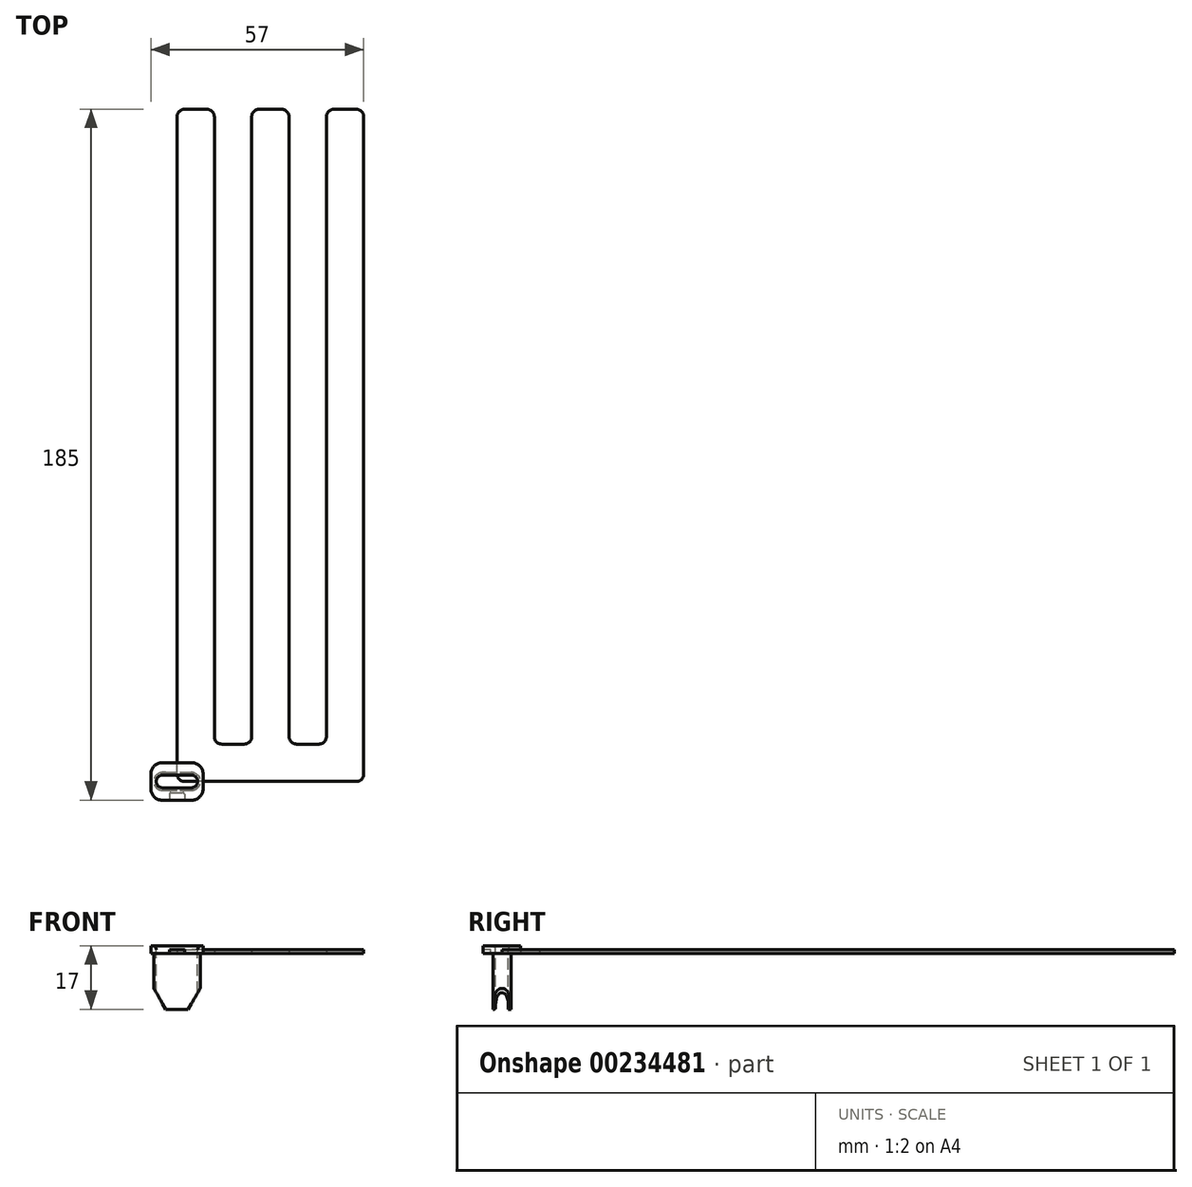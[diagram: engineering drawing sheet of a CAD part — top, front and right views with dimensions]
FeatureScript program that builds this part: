
annotation { "Feature Type Name" : "Feature", "Feature Type Description" : "" }
export const myFeature = defineFeature(function(context is Context, id is Id, definition is map)
    precondition{}
    {
        {
            var Q0;
            Q0=qCreatedBy(makeId("Top.planeOp"),FACE);
            var sketch = newSketch(context, id + "F0", { "sketchPlane" : qUnion([Q0])});
            skLineSegment(sketch, "E0", {"start": v(-3.85, 0) * mm, "end": v(3.85, 0) * mm});
            skArc(sketch, "E1.0.startCap", {"start": v(-3.85, -2.4) * mm, "mid": v(-6.25, 0) * mm, "end": v(-3.85, 2.4) * mm});
            skArc(sketch, "E1.0.endCap", {"start": v(3.85, 2.4) * mm, "mid": v(6.25, 0) * mm, "end": v(3.85, -2.4) * mm});
            skLineSegment(sketch, "E1.0.left", {"start": v(-3.85, 2.4) * mm, "end": v(3.85, 2.4) * mm});
            skLineSegment(sketch, "E1.0.right", {"start": v(-3.85, -2.4) * mm, "end": v(3.85, -2.4) * mm});
            skLineSegment(sketch, "E2.0", {"start": v(-3.85, 1.7) * mm, "end": v(3.85, 1.7) * mm});
            skArc(sketch, "E2.1", {"start": v(-3.85, -1.7) * mm, "mid": v(-5.55, 0) * mm, "end": v(-3.85, 1.7) * mm});
            skLineSegment(sketch, "E2.2", {"start": v(-3.85, -1.7) * mm, "end": v(3.85, -1.7) * mm});
            skArc(sketch, "E2.3", {"start": v(3.85, 1.7) * mm, "mid": v(5.55, 0) * mm, "end": v(3.85, -1.7) * mm});
            skSolve(sketch);
        }
        {
            var Q0;
            Q0 = qSketchRegion(id + "F0", true);
            extrude(context, id + "F1", {"entities" : qUnion([Q0]), "oppositeDirection" : true, "depth" : 15 * mm, "offsetDistance" : 25 * mm});
        }
        {
            var Q0;
            Q0=qCreatedBy(makeId("Top.planeOp"),FACE);
            var sketch = newSketch(context, id + "F2", { "sketchPlane" : qUnion([Q0])});
            skArc(sketch, "E3.0", {"start": v(-3.85, -1.7) * mm, "mid": v(-5.55, 0) * mm, "end": v(-3.85, 1.7) * mm});
            skLineSegment(sketch, "E4.0", {"start": v(-3.85, 1.7) * mm, "end": v(3.85, 1.7) * mm});
            skArc(sketch, "E5.0", {"start": v(3.85, 1.7) * mm, "mid": v(5.55, 0) * mm, "end": v(3.85, -1.7) * mm});
            skLineSegment(sketch, "E6.0", {"start": v(-3.85, -1.7) * mm, "end": v(3.85, -1.7) * mm});
            skLineSegment(sketch, "E7.bottom", {"start": v(-7, 5) * mm, "end": v(7, 5) * mm});
            skLineSegment(sketch, "E7.top", {"start": v(-7, -5) * mm, "end": v(7, -5) * mm});
            skLineSegment(sketch, "E7.left", {"start": v(-7, 5) * mm, "end": v(-7, -5) * mm});
            skLineSegment(sketch, "E7.right", {"start": v(7, 5) * mm, "end": v(7, -5) * mm});
            skPoint(sketch, "E7.middle", {"position": v(0, 0) * mm});
            skSolve(sketch);
        }
        {
            var Q0;
            Q0 = qSketchRegion(id + "F2", true);
            extrude(context, id + "F3", {"entities" : qUnion([Q0]), "operationType" : NewBodyOperationType.ADD, "depth" : 2 * mm, "offsetDistance" : 25 * mm});
        }
        {
            var Q0;
            Q0=makeQuery(id+"F3.opExtrude","SWEPT_EDGE",EDGE,{"disambiguationData":[OSD([sQuery(id+"F2.wireOp",EDGE,"E7.top"),sQuery(id+"F2.wireOp",EDGE,"E7.left")])]});
            var Q1;
            Q1=makeQuery(id+"F3.opExtrude","SWEPT_EDGE",EDGE,{"disambiguationData":[OSD([sQuery(id+"F2.wireOp",EDGE,"E7.top"),sQuery(id+"F2.wireOp",EDGE,"E7.right")])]});
            var Q2;
            Q2=makeQuery(id+"F3.opExtrude","SWEPT_EDGE",EDGE,{"disambiguationData":[OSD([sQuery(id+"F2.wireOp",EDGE,"E7.bottom"),sQuery(id+"F2.wireOp",EDGE,"E7.right")])]});
            var Q3;
            Q3=makeQuery(id+"F3.opExtrude","SWEPT_EDGE",EDGE,{"disambiguationData":[OSD([sQuery(id+"F2.wireOp",EDGE,"E7.bottom"),sQuery(id+"F2.wireOp",EDGE,"E7.left")])]});
            fillet(context, id + "F4", {"entities" : qUnion([Q0, Q1, Q2, Q3]), "tangentPropagation" : true, "radius" : 3 * mm, "defaultsChanged" : true, "vertexSettings" : [], "allowEdgeOverflow" : false});
        }
        {
            var Q0;
            Q0=qCreatedBy(makeId("Front.planeOp"),FACE);
            var sketch = newSketch(context, id + "F5", { "sketchPlane" : qUnion([Q0])});
            skLineSegment(sketch, "E8.0", {"start": v(-3.85, -15) * mm, "end": v(3.85, -15) * mm, "construction": true});
            skLineSegment(sketch, "E9", {"start": v(-3, -15) * mm, "end": v(-8.4, -5.66) * mm});
            skLineSegment(sketch, "E10", {"start": v(-8.4, -5.66) * mm, "end": v(-8.4, -15) * mm});
            skLineSegment(sketch, "E11", {"start": v(-8.4, -15) * mm, "end": v(-3, -15) * mm});
            skLineSegment(sketch, "E12", {"start": v(3, -15) * mm, "end": v(8.4, -5.66) * mm});
            skLineSegment(sketch, "E13", {"start": v(8.4, -5.66) * mm, "end": v(8.4, -15) * mm});
            skLineSegment(sketch, "E14", {"start": v(8.4, -15) * mm, "end": v(3, -15) * mm});
            skSolve(sketch);
        }
        {
            var Q0;
            Q0 = qSketchRegion(id + "F5", true);
            extrude(context, id + "F6", {"entities" : qUnion([Q0]), "operationType" : NewBodyOperationType.REMOVE, "endBound" : BoundingType.THROUGH_ALL, "oppositeDirection" : true, "depth" : 25 * mm, "offsetDistance" : 25 * mm, "hasSecondDirection" : true, "secondDirectionBound" : BoundingType.THROUGH_ALL, "secondDirectionOppositeDirection" : false, "secondDirectionDepth" : 25 * mm});
        }
        {
            var Q0;
            Q0=makeQuery(id+"F3.opExtrude","CAP_EDGE",EDGE,{"disambiguationData":[OSD([sQuery(id+"F2.wireOp",EDGE,"E3.0")])],"isStart":false});
            var Q1;
            {var subQ1=sQuery(id+"F0.wireOp",EDGE,"E1.0.right");var subQ2=sQuery(id+"F5.wireOp",EDGE,"E9");Q1=makeQuery(id+"F6.boolean.opBoolean","COPY",EDGE,{"disambiguationData":[TD([makeQuery(id+"F1.opExtrude","SWEPT_FACE",FACE,{"disambiguationData":[OSD([subQ1])]})])],"derivedFrom":makeQuery(id+"F6.opExtrude","SWEPT_EDGE",EDGE,{"disambiguationData":[OSD([subQ2,sQuery(id+"F5.wireOp",EDGE,"E11")])]})});}
            var Q2;
            {var subQ1=sQuery(id+"F0.wireOp",EDGE,"E1.0.right");var subQ2=sQuery(id+"F5.wireOp",EDGE,"E12");Q2=makeQuery(id+"F6.boolean.opBoolean","COPY",EDGE,{"disambiguationData":[TD([makeQuery(id+"F1.opExtrude","SWEPT_FACE",FACE,{"disambiguationData":[OSD([subQ1])]})])],"derivedFrom":makeQuery(id+"F6.opExtrude","SWEPT_EDGE",EDGE,{"disambiguationData":[OSD([subQ2,sQuery(id+"F5.wireOp",EDGE,"E14")])]})});}
            var Q3;
            {var subQ0=sQuery(id+"F0.wireOp",EDGE,"E1.0.left");var subQ1=sQuery(id+"F5.wireOp",EDGE,"E12");Q3=makeQuery(id+"F6.boolean.opBoolean","COPY",EDGE,{"disambiguationData":[TD([makeQuery(id+"F1.opExtrude","SWEPT_FACE",FACE,{"disambiguationData":[OSD([subQ0])]})])],"derivedFrom":makeQuery(id+"F6.opExtrude","SWEPT_EDGE",EDGE,{"disambiguationData":[OSD([subQ1,sQuery(id+"F5.wireOp",EDGE,"E14")])]})});}
            var Q4;
            {var subQ0=sQuery(id+"F0.wireOp",EDGE,"E1.0.left");var subQ2=sQuery(id+"F5.wireOp",EDGE,"E9");Q4=makeQuery(id+"F6.boolean.opBoolean","COPY",EDGE,{"disambiguationData":[TD([makeQuery(id+"F1.opExtrude","SWEPT_FACE",FACE,{"disambiguationData":[OSD([subQ0])]})])],"derivedFrom":makeQuery(id+"F6.opExtrude","SWEPT_EDGE",EDGE,{"disambiguationData":[OSD([subQ2,sQuery(id+"F5.wireOp",EDGE,"E11")])]})});}
            fillet(context, id + "F7", {"entities" : qUnion([Q0, Q1, Q2, Q3, Q4]), "tangentPropagation" : true, "radius" : 1 * mm, "defaultsChanged" : false, "vertexSettings" : [], "allowEdgeOverflow" : false});
        }
        {
            var Q0;
            Q0=makeQuery(id+"F3.opExtrude","SWEPT_FACE",FACE,{"disambiguationData":[OSD([sQuery(id+"F2.wireOp",EDGE,"E7.top")])]});
            var sketch = newSketch(context, id + "F8", { "sketchPlane" : qUnion([Q0])});
            skLineSegment(sketch, "E15.bottom", {"start": v(-2, 0) * mm, "end": v(2, 0) * mm});
            skLineSegment(sketch, "E15.top", {"start": v(-2, 1) * mm, "end": v(2, 1) * mm});
            skLineSegment(sketch, "E15.left", {"start": v(-2, 0) * mm, "end": v(-2, 1) * mm});
            skLineSegment(sketch, "E15.right", {"start": v(2, 0) * mm, "end": v(2, 1) * mm});
            skSolve(sketch);
        }
        {
            var Q0;
            Q0 = qSketchRegion(id + "F8", true);
            extrude(context, id + "F9", {"entities" : qUnion([Q0]), "operationType" : NewBodyOperationType.REMOVE, "oppositeDirection" : true, "depth" : 2 * mm, "offsetDistance" : 25 * mm});
        }
        {
            var Q0;
            Q0=makeQuery(id+"F1.opExtrude","CAP_EDGE",EDGE,{"disambiguationData":[OSD([sQuery(id+"F0.wireOp",EDGE,"E2.2")])],"isStart":false});
            var Q1;
            Q1=makeQuery(id+"F1.opExtrude","CAP_EDGE",EDGE,{"disambiguationData":[OSD([sQuery(id+"F0.wireOp",EDGE,"E1.0.right")])],"isStart":true});
            var Q2;
            Q2=makeQuery(id+"F9.boolean.opBoolean","COPY",EDGE,{"derivedFrom":makeQuery(id+"F9.opExtrude","CAP_EDGE",EDGE,{"disambiguationData":[OSD([sQuery(id+"F8.wireOp",EDGE,"E15.left")])],"isStart":false})});
            var Q3;
            Q3=makeQuery(id+"F9.boolean.opBoolean","COPY",EDGE,{"derivedFrom":makeQuery(id+"F9.opExtrude","CAP_EDGE",EDGE,{"disambiguationData":[OSD([sQuery(id+"F8.wireOp",EDGE,"E15.right")])],"isStart":false})});
            var Q4;
            Q4=makeQuery(id+"F9.boolean.opBoolean","COPY",EDGE,{"derivedFrom":makeQuery(id+"F9.opExtrude","CAP_EDGE",EDGE,{"disambiguationData":[OSD([sQuery(id+"F8.wireOp",EDGE,"E15.right")])],"isStart":true})});
            var Q5;
            Q5=makeQuery(id+"F9.boolean.opBoolean","COPY",EDGE,{"derivedFrom":makeQuery(id+"F9.opExtrude","CAP_EDGE",EDGE,{"disambiguationData":[OSD([sQuery(id+"F8.wireOp",EDGE,"E15.left")])],"isStart":true})});
            var Q6;
            Q6=makeQuery(id+"FBNVAN4CYz6kUtZ_1.1.F9.boolean.opBoolean","COPY",EDGE,{"derivedFrom":makeQuery(id+"FBNVAN4CYz6kUtZ_1.1.F9.opExtrude","CAP_EDGE",EDGE,{"disambiguationData":[OSD([sQuery(id+"F8.wireOp",EDGE,"E15.left")])],"isStart":true})});
            var Q7;
            Q7=makeQuery(id+"FBNVAN4CYz6kUtZ_1.1.F9.boolean.opBoolean","COPY",EDGE,{"derivedFrom":makeQuery(id+"FBNVAN4CYz6kUtZ_1.1.F9.opExtrude","CAP_EDGE",EDGE,{"disambiguationData":[OSD([sQuery(id+"F8.wireOp",EDGE,"E15.left")])],"isStart":false})});
            var Q8;
            Q8=makeQuery(id+"FBNVAN4CYz6kUtZ_1.1.F9.boolean.opBoolean","COPY",EDGE,{"derivedFrom":makeQuery(id+"FBNVAN4CYz6kUtZ_1.1.F9.opExtrude","CAP_EDGE",EDGE,{"disambiguationData":[OSD([sQuery(id+"F8.wireOp",EDGE,"E15.right")])],"isStart":true})});
            var Q9;
            Q9=makeQuery(id+"FBNVAN4CYz6kUtZ_1.1.F9.boolean.opBoolean","COPY",EDGE,{"derivedFrom":makeQuery(id+"FBNVAN4CYz6kUtZ_1.1.F9.opExtrude","CAP_EDGE",EDGE,{"disambiguationData":[OSD([sQuery(id+"F8.wireOp",EDGE,"E15.right")])],"isStart":false})});
            fillet(context, id + "F10", {"entities" : qUnion([Q0, Q1, Q2, Q3, Q4, Q5, Q6, Q7, Q8, Q9]), "tangentPropagation" : true, "radius" : 0.4 * mm, "defaultsChanged" : false, "vertexSettings" : [], "allowEdgeOverflow" : false});
        }
        {
            var Q0;
            Q0=qCreatedBy(makeId("Top.planeOp"),FACE);
            var sketch = newSketch(context, id + "F11", { "sketchPlane" : qUnion([Q0])});
            skLineSegment(sketch, "E16", {"start": v(0, 0) * mm, "end": v(0, 180) * mm});
            skLineSegment(sketch, "E17", {"start": v(0, 180) * mm, "end": v(10, 180) * mm});
            skLineSegment(sketch, "E18", {"start": v(10, 180) * mm, "end": v(10, 10) * mm});
            skLineSegment(sketch, "E19", {"start": v(10, 10) * mm, "end": v(20, 10) * mm});
            skLineSegment(sketch, "E20", {"start": v(20, 10) * mm, "end": v(20, 180) * mm});
            skLineSegment(sketch, "E21", {"start": v(20, 180) * mm, "end": v(30, 180) * mm});
            skLineSegment(sketch, "E22", {"start": v(30, 180) * mm, "end": v(30, 10) * mm});
            skLineSegment(sketch, "E23", {"start": v(30, 10) * mm, "end": v(40, 10) * mm});
            skLineSegment(sketch, "E24", {"start": v(40, 10) * mm, "end": v(40, 180) * mm});
            skLineSegment(sketch, "E25", {"start": v(40, 180) * mm, "end": v(50, 180) * mm});
            skLineSegment(sketch, "E26", {"start": v(50, 180) * mm, "end": v(50, 0) * mm});
            skLineSegment(sketch, "E27", {"start": v(50, 0) * mm, "end": v(0, 0) * mm});
            skSolve(sketch);
        }
        {
            var Q0;
            Q0 = qSketchRegion(id + "F11", true);
            extrude(context, id + "F12", {"entities" : qUnion([Q0]), "depth" : 1 * mm, "offsetDistance" : 25 * mm});
        }
        {
            var Q0;
            Q0=makeQuery(id+"F12.opExtrude","SWEPT_EDGE",EDGE,{"disambiguationData":[OSD([sQuery(id+"F11.wireOp",EDGE,"E26"),sQuery(id+"F11.wireOp",EDGE,"E27")])]});
            var Q1;
            Q1=makeQuery(id+"F12.opExtrude","SWEPT_EDGE",EDGE,{"disambiguationData":[OSD([sQuery(id+"F11.wireOp",EDGE,"E16"),sQuery(id+"F11.wireOp",EDGE,"E27")])]});
            var Q2;
            Q2=makeQuery(id+"F12.opExtrude","SWEPT_EDGE",EDGE,{"disambiguationData":[OSD([sQuery(id+"F11.wireOp",EDGE,"E24"),sQuery(id+"F11.wireOp",EDGE,"E25")])]});
            var Q3;
            Q3=makeQuery(id+"F12.opExtrude","SWEPT_EDGE",EDGE,{"disambiguationData":[OSD([sQuery(id+"F11.wireOp",EDGE,"E20"),sQuery(id+"F11.wireOp",EDGE,"E21")])]});
            var Q4;
            Q4=makeQuery(id+"F12.opExtrude","SWEPT_EDGE",EDGE,{"disambiguationData":[OSD([sQuery(id+"F11.wireOp",EDGE,"E16"),sQuery(id+"F11.wireOp",EDGE,"E17")])]});
            var Q5;
            Q5=makeQuery(id+"F12.opExtrude","SWEPT_EDGE",EDGE,{"disambiguationData":[OSD([sQuery(id+"F11.wireOp",EDGE,"E17"),sQuery(id+"F11.wireOp",EDGE,"E18")])]});
            var Q6;
            Q6=makeQuery(id+"F12.opExtrude","SWEPT_EDGE",EDGE,{"disambiguationData":[OSD([sQuery(id+"F11.wireOp",EDGE,"E21"),sQuery(id+"F11.wireOp",EDGE,"E22")])]});
            var Q7;
            Q7=makeQuery(id+"F12.opExtrude","SWEPT_EDGE",EDGE,{"disambiguationData":[OSD([sQuery(id+"F11.wireOp",EDGE,"E25"),sQuery(id+"F11.wireOp",EDGE,"E26")])]});
            var Q8;
            Q8=makeQuery(id+"F12.opExtrude","SWEPT_EDGE",EDGE,{"disambiguationData":[OSD([sQuery(id+"F11.wireOp",EDGE,"E23"),sQuery(id+"F11.wireOp",EDGE,"E24")])]});
            var Q9;
            Q9=makeQuery(id+"F12.opExtrude","SWEPT_EDGE",EDGE,{"disambiguationData":[OSD([sQuery(id+"F11.wireOp",EDGE,"E19"),sQuery(id+"F11.wireOp",EDGE,"E20")])]});
            var Q10;
            Q10=makeQuery(id+"F12.opExtrude","SWEPT_EDGE",EDGE,{"disambiguationData":[OSD([sQuery(id+"F11.wireOp",EDGE,"E18"),sQuery(id+"F11.wireOp",EDGE,"E19")])]});
            var Q11;
            Q11=makeQuery(id+"F12.opExtrude","SWEPT_EDGE",EDGE,{"disambiguationData":[OSD([sQuery(id+"F11.wireOp",EDGE,"E22"),sQuery(id+"F11.wireOp",EDGE,"E23")])]});
            fillet(context, id + "F13", {"entities" : qUnion([Q0, Q1, Q2, Q3, Q4, Q5, Q6, Q7, Q8, Q9, Q10, Q11]), "tangentPropagation" : true, "radius" : 2 * mm, "defaultsChanged" : false, "vertexSettings" : [], "allowEdgeOverflow" : false});
        }
    });
